# Revit family: 306_d5d358939b3541c694e5ccdd564967
name_source: partatom
category: Pipe Accessories
units: mm (PartAtom-declared; Revit-internal decimal feet)

## family parameters
Always vertical = Yes
Cut with Voids When Loaded = No
Part Type = Valve - Breaks Into
Round Connector Dimension = Use Diameter
Shared = No
Work Plane-Based = No

## types (3) — shared parameters
Description = 2-way Motorized ball valve MBA121, PN32 internal thread
H1 = 1 mm  [stored 0.00328084 ft]
L2D_Min = 3048 mm
Manufacturer = ESBE
QmdConnectorList = 301;D;302;D
URL = http://www.esbe.eu
X11 = 17 mm
X11__ve = -17 mm
Y0 = 5 mm  [stored 0.0164042 ft]
Y11 = 3 mm  [stored 0.00984252 ft]
Z3 = 11 mm
Z4 = 52 mm
Z6 = 35 mm
Z6__ve = -35 mm
Z7 = 3 mm  [stored 0.00984252 ft]
magiPartTypeId = 306
magiProductFamilyId = d5d358939b3541c694e5ccdd564967

## per-type parameters (varying)
| type | D | E | L2D | W2D | X1 | X12 | X12__ve | X14 | X5 | X6 | X7 | X8 | Y10 | Y10__ve | Y12 | Y2 | Y3 | Y4 | Y5 | Z2 | Z2__ve | Z5 | magiProductCode | magiProductId |
| MBA121 G1  FF 230VAC 2-P 10NM | 25 mm | 29 mm  [stored 0.0951444 ft] | 82 mm | 25 mm  [stored 0.082021 ft] | 41 mm  [stored 0.134514 ft] | 27 mm | -27 mm | 41 mm  [stored 0.134514 ft] | 2 mm  [stored 0.00656168 ft] | 4 mm  [stored 0.0131234 ft] | 7 mm  [stored 0.0229659 ft] | 19 mm | 19 mm | -19 mm | 12 mm  [stored 0.0393701 ft] | 13 mm  [stored 0.0426509 ft] | 14 mm  [stored 0.0459318 ft] | 15 mm  [stored 0.0492126 ft] | 16 mm | 26 mm | -26 mm | 3 mm  [stored 0.00984252 ft] | MBA121 G1" FF 230VAC 2-P 10NM | 9bb2f2e6a08d47dc9dc2bea2a88609 |
| MBA121 G3/4  FF 230VAC 2-P 10NM | 20 mm | 25 mm  [stored 0.082021 ft] | 68 mm | 20 mm  [stored 0.0656168 ft] | 34 mm | 19 mm | -19 mm | 34 mm | 2 mm  [stored 0.00656168 ft] | 3 mm  [stored 0.00984252 ft] | 6 mm  [stored 0.019685 ft] | 16 mm | 15 mm  [stored 0.0492126 ft] | -15 mm | 10 mm  [stored 0.0328084 ft] | 10 mm  [stored 0.0328084 ft] | 11 mm | 12 mm  [stored 0.0393701 ft] | 12 mm  [stored 0.0393701 ft] | 23 mm | -23 mm | 2 mm  [stored 0.00656168 ft] | MBA121 G3/4" FF 230VAC 2-P 10NM | 49a47f68358f497a84cfb4f724ffb5 |
| MBA121 G11/4 FF 230VAC 2-P 10NM | 32 mm | 34 mm | 86 mm | 32 mm | 43 mm | 29 mm  [stored 0.0951444 ft] | -29 mm | 43 mm | 3 mm  [stored 0.00984252 ft] | 4 mm  [stored 0.0131234 ft] | 8 mm  [stored 0.0262467 ft] | 20 mm  [stored 0.0656168 ft] | 24 mm | -24 mm | 16 mm | 17 mm | 18 mm | 19 mm | 20 mm  [stored 0.0656168 ft] | 31 mm  [stored 0.101706 ft] | -31 mm  [stored -0.101706 ft] | 3 mm  [stored 0.00984252 ft] | MBA121 G11/4 FF 230VAC 2-P 10NM | 84b419aeadf84addbcec071cb61316 |

note: [stored X ft] marks values corroborated as IEEE doubles in the binary element streams (Revit-internal decimal feet)

## geometry (parser evidence)
native form markers: Sweep x3
no freeform markers — native parametric forms only
